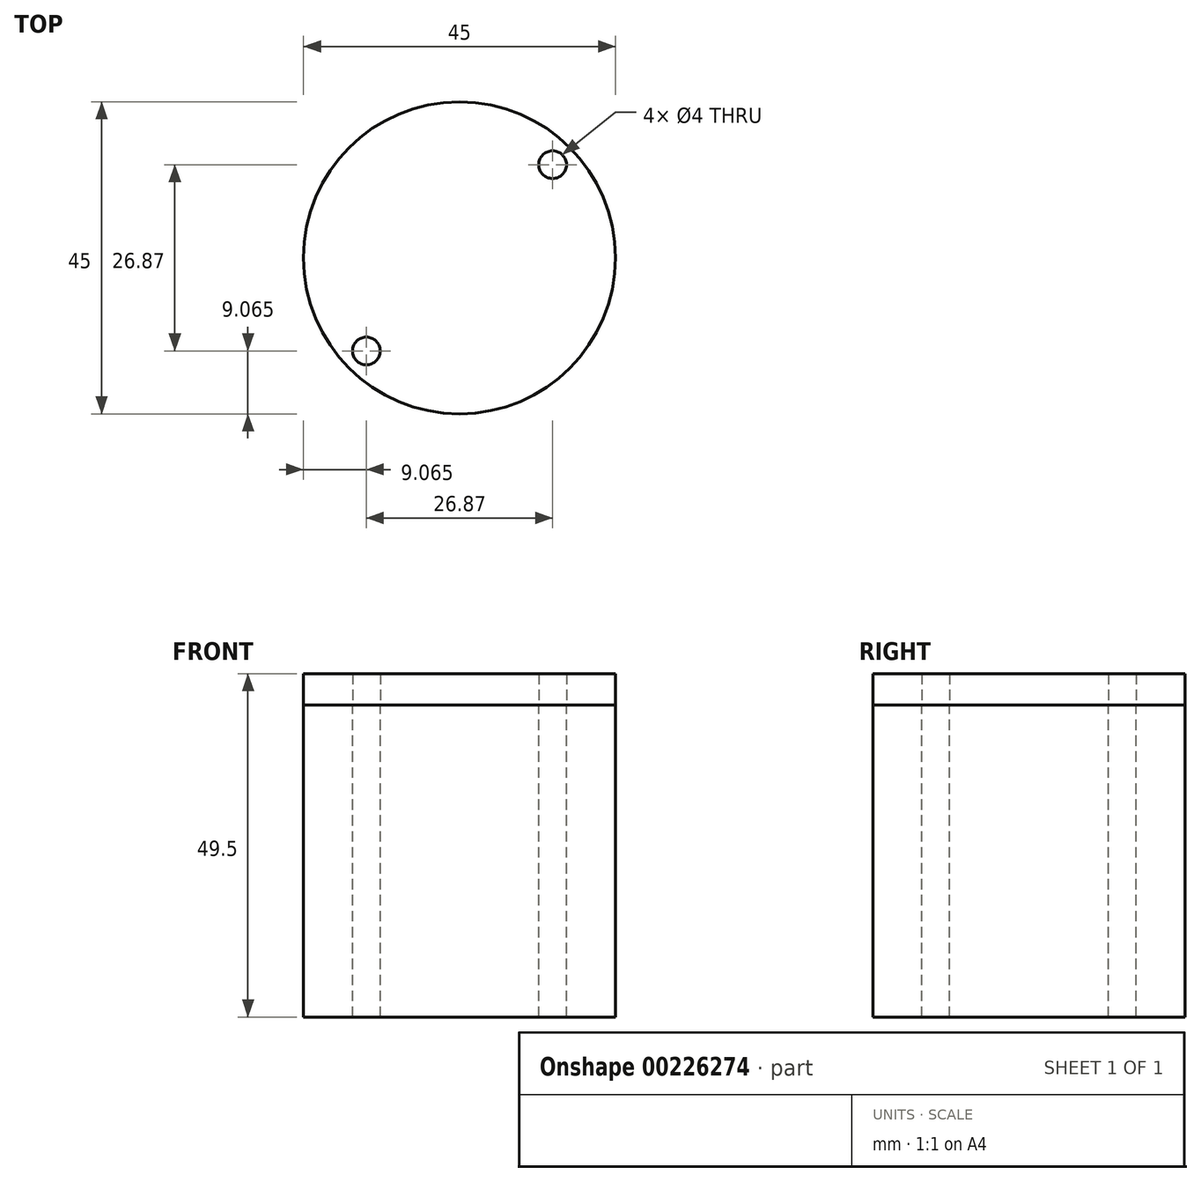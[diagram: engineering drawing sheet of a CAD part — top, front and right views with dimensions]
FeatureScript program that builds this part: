
annotation { "Feature Type Name" : "Feature", "Feature Type Description" : "" }
export const myFeature = defineFeature(function(context is Context, id is Id, definition is map)
    precondition{}
    {
        {
            var Q0;
            Q0=qCreatedBy(makeId("Top.planeOp"),FACE);
            var sketch = newSketch(context, id + "F0", { "sketchPlane" : qUnion([Q0])});
            skCircle(sketch, "E0", {"center": v(0, 0) * mm, "radius": 22.5 * mm});
            skCircle(sketch, "E1", {"center": v(-13.44, 13.44) * mm, "radius": 2 * mm});
            skCircle(sketch, "E2.MirrorC", {"center": v(13.44, 13.44) * mm, "radius": 2 * mm});
            skCircle(sketch, "E3.MirrorC", {"center": v(-13.44, -13.44) * mm, "radius": 2 * mm});
            skCircle(sketch, "E4.MirrorC", {"center": v(13.44, -13.44) * mm, "radius": 2 * mm});
            skSolve(sketch);
        }
        {
            var Q0;
            Q0=makeQuery(id+"F0.imprint","IMPRINT",FACE,{"disambiguationData":[TD([[makeQuery(id+"F0.imprint","IMPRINT",EDGE,{"derivedFrom":sQuery(id+"F0.wireOp",EDGE,"E1")}),-1.0]])]});
            var Q1;
            Q1=makeQuery(id+"F0.imprint","IMPRINT",FACE,{"disambiguationData":[TD([[makeQuery(id+"F0.imprint","IMPRINT",EDGE,{"derivedFrom":sQuery(id+"F0.wireOp",EDGE,"E1")}),1.0]])]});
            var Q2;
            Q2=makeQuery(id+"F0.imprint","IMPRINT",FACE,{"disambiguationData":[TD([[makeQuery(id+"F0.imprint","IMPRINT",EDGE,{"derivedFrom":sQuery(id+"F0.wireOp",EDGE,"E2.MirrorC")}),-1.0]])]});
            var Q3;
            Q3=makeQuery(id+"F0.imprint","IMPRINT",FACE,{"disambiguationData":[TD([[makeQuery(id+"F0.imprint","IMPRINT",EDGE,{"derivedFrom":sQuery(id+"F0.wireOp",EDGE,"E3.MirrorC")}),-1.0]])]});
            var Q4;
            Q4=makeQuery(id+"F0.imprint","IMPRINT",FACE,{"disambiguationData":[TD([[makeQuery(id+"F0.imprint","IMPRINT",EDGE,{"derivedFrom":sQuery(id+"F0.wireOp",EDGE,"E4.MirrorC")}),1.0]])]});
            extrude(context, id + "F1", {"entities" : qUnion([Q0, Q1, Q2, Q3, Q4]), "depth" : 4.5 * mm});
        }
        {
            var Q0;
            Q0=makeQuery(id+"F0.imprint","IMPRINT",FACE,{"disambiguationData":[TD([[makeQuery(id+"F0.imprint","IMPRINT",EDGE,{"derivedFrom":sQuery(id+"F0.wireOp",EDGE,"E3.MirrorC")}),-1.0]])]});
            var Q1;
            Q1=makeQuery(id+"F0.imprint","IMPRINT",FACE,{"disambiguationData":[TD([[makeQuery(id+"F0.imprint","IMPRINT",EDGE,{"derivedFrom":sQuery(id+"F0.wireOp",EDGE,"E4.MirrorC")}),1.0]])]});
            var Q2;
            Q2=makeQuery(id+"F0.imprint","IMPRINT",FACE,{"disambiguationData":[TD([[makeQuery(id+"F0.imprint","IMPRINT",EDGE,{"derivedFrom":sQuery(id+"F0.wireOp",EDGE,"E1")}),1.0]])]});
            var Q3;
            Q3=makeQuery(id+"F0.imprint","IMPRINT",FACE,{"disambiguationData":[TD([[makeQuery(id+"F0.imprint","IMPRINT",EDGE,{"derivedFrom":sQuery(id+"F0.wireOp",EDGE,"E2.MirrorC")}),-1.0]])]});
            extrude(context, id + "F2", {"entities" : qUnion([Q0, Q1, Q2, Q3]), "oppositeDirection" : true, "depth" : 45 * mm});
        }
    });
